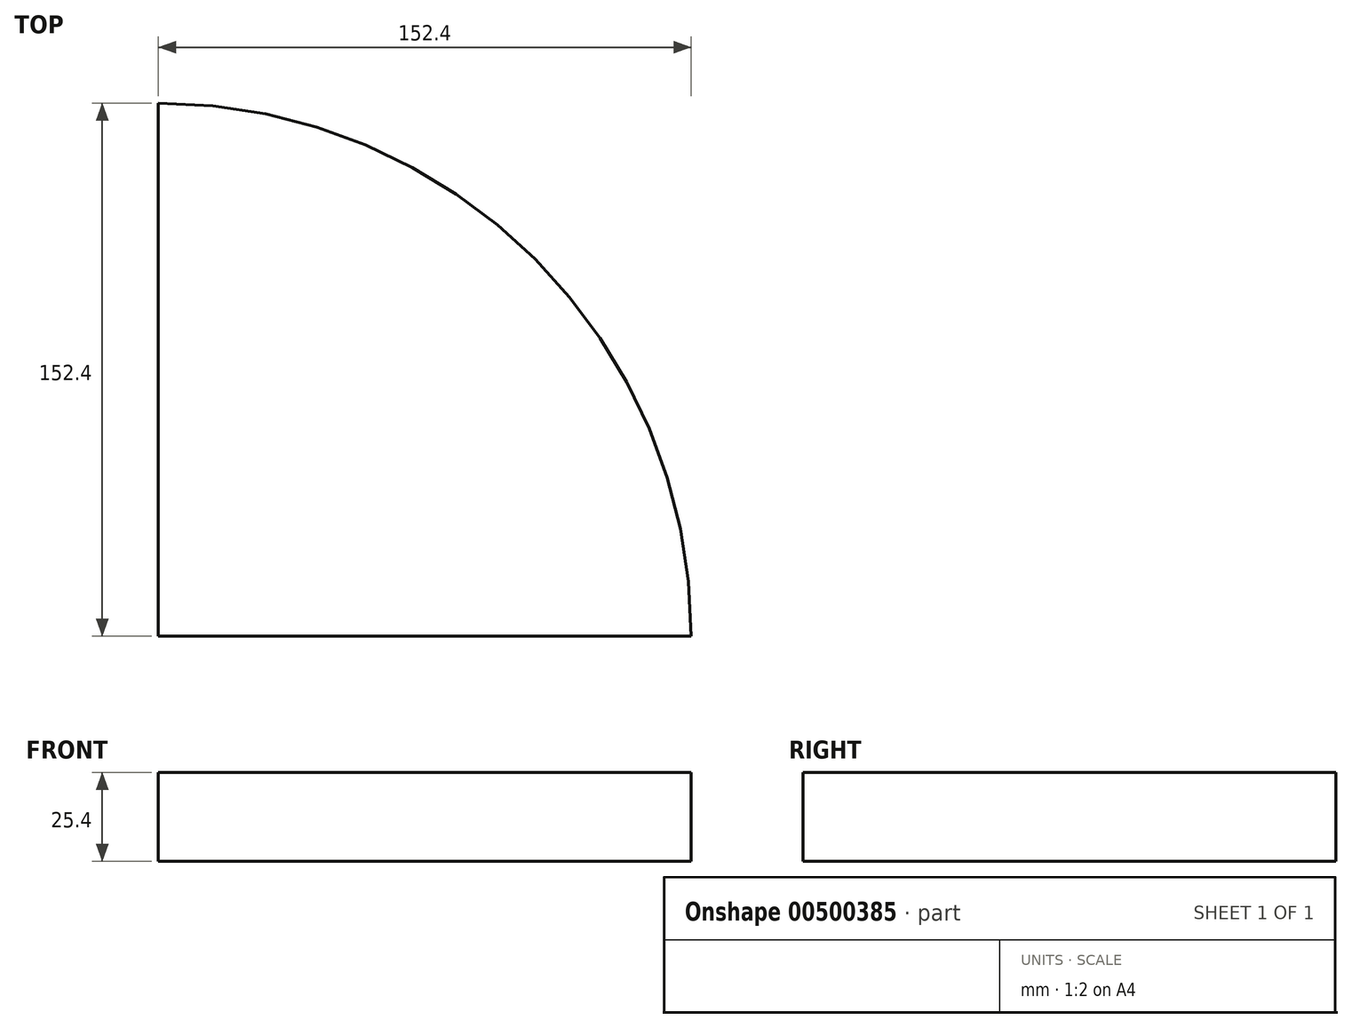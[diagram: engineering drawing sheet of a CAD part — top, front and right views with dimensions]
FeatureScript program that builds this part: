
annotation { "Feature Type Name" : "Feature", "Feature Type Description" : "" }
export const myFeature = defineFeature(function(context is Context, id is Id, definition is map)
    precondition{}
    {
        {
            var Q0;
            Q0=qCreatedBy(makeId("Top.planeOp"),FACE);
            var sketch = newSketch(context, id + "F0", { "sketchPlane" : qUnion([Q0])});
            skLineSegment(sketch, "E0.bottom", {"start": v(0, 0) * mm, "end": v(152.4, 0) * mm});
            skLineSegment(sketch, "E0.top", {"start": v(0, 152.4) * mm, "end": v(152.4, 152.4) * mm, "construction": true});
            skLineSegment(sketch, "E0.left", {"start": v(0, 0) * mm, "end": v(0, 152.4) * mm});
            skLineSegment(sketch, "E0.right", {"start": v(152.4, 0) * mm, "end": v(152.4, 152.4) * mm, "construction": true});
            skArc(sketch, "E1", {"start": v(152.4, 0) * mm, "mid": v(107.76, 107.76) * mm, "end": v(0, 152.4) * mm});
            skSolve(sketch);
        }
        {
            var Q0;
            Q0=makeQuery(id+"F0.imprint","IMPRINT",FACE,{"disambiguationData":[TD([[makeQuery(id+"F0.imprint","IMPRINT",EDGE,{"derivedFrom":sQuery(id+"F0.wireOp",EDGE,"E0.bottom")}),1.0]])]});
            var Q1;
            Q1=sQuery(id+"F0.wireOp",EDGE,"E0.top");
            var Q2;
            Q2=sQuery(id+"F0.wireOp",EDGE,"E0.right");
            extrude(context, id + "F1", {"entities" : qUnion([Q0]), "surfaceEntities" : qUnion([Q1, Q2]), "depth" : 25.4 * mm});
        }
    });
